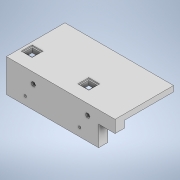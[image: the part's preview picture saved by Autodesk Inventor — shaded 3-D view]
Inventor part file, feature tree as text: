
AUTODESK INVENTOR PART (.ipt)
format: ipt  version: 2020 (Build 240168000, 168)  size: 354,816 bytes
history: native  units: mm
features: reference x18, projected_geometry x17, other x12, sketch x12, extrude x10, hole x2
ambient origin geometry x8: Origin, YZ Plane, XZ Plane, XY Plane, X Axis, Y Axis, Z Axis, Center Point
bodies: Body1 (feature_tree)
feature tree (71):
  other  "솔리드1"
  extrude  "돌출1"  Depth=60.0mm
  extrude  "돌출2"  Depth=10.0mm
  other  "작업 평면1"
  extrude  "돌출3"  Depth=10.0mm TaperAngle=0.0deg
  sketch  "스케치4"
  other  "작업 평면2"
  extrude  "돌출4"  Depth=16.193009mm
  extrude  "돌출7"  Depth=40.0mm
  extrude  "돌출8"  TaperAngle=0.0deg  [1 undecoded]
  extrude  "돌출9"  Depth=50.0mm
  sketch  "스케치11"
  extrude  "돌출10"  Depth=10.0mm TaperAngle=0.0deg
  extrude  "돌출11"  Depth=60.0mm TaperAngle=0.0deg
  hole  "구멍1"  [1 undecoded]
  extrude  "돌출12"  Depth=30.0mm TaperAngle=0.0deg
  hole  "구멍2"  [1 undecoded]
  sketch  "스케치1"
  reference  "참조1"
  reference  "참조2"
  reference  "참조3"
  reference  "참조4"
  reference  "참조5"
  reference  "참조6"
  sketch  "스케치2"
  projected_geometry  "투영된 루프1"
  reference  "참조7"
  reference  "참조8"
  sketch  "스케치3"
  projected_geometry  "투영된 루프2"
  reference  "참조9"
  reference  "참조10"
  reference  "참조11"
  reference  "참조12"
  reference  "참조13"
  reference  "참조14"
  projected_geometry  "투영된 루프3"
  projected_geometry  "투영된 루프4"
  reference  "참조15"
  reference  "참조16"
  projected_geometry  "투영된 루프8"
  sketch  "스케치7"
  reference  "참조17"
  reference  "참조18"
  projected_geometry  "투영된 루프9"
  sketch  "스케치9"
  projected_geometry  "투영된 루프11"
  sketch  "스케치10"
  projected_geometry  "투영된 루프12"
  projected_geometry  "투영된 루프13"
  projected_geometry  "투영된 루프14"
  projected_geometry  "투영된 루프15"
  sketch  "스케치12"
  projected_geometry  "투영된 루프16"
  sketch  "스케치13"
  projected_geometry  "투영된 루프17"
  projected_geometry  "투영된 루프18"
  sketch  "스케치14"
  projected_geometry  "투영된 루프19"
  sketch  "스케치15"
  projected_geometry  "투영된 루프20"
  projected_geometry  "투영된 루프21"
  other  "<userpath>\Documents\Inventor\CoMoVi\Package\v4.iam"
  other  "v4.iam"
  other  "cross_AL_profile:2"
  other  "Bumper_assey2:2"
  other  "bumper_final_6:1"
  other  "cross_AL_profile:1"
  other  "wheel:1"
  other  "Bumper_assey2:1"
  other  "bumper_final_3:1"
note: 3 required parameter values undecoded (feature->parameter linkage not recoverable at this tier; creation-order binding heuristic only, values carry confidence <= 0.55)
